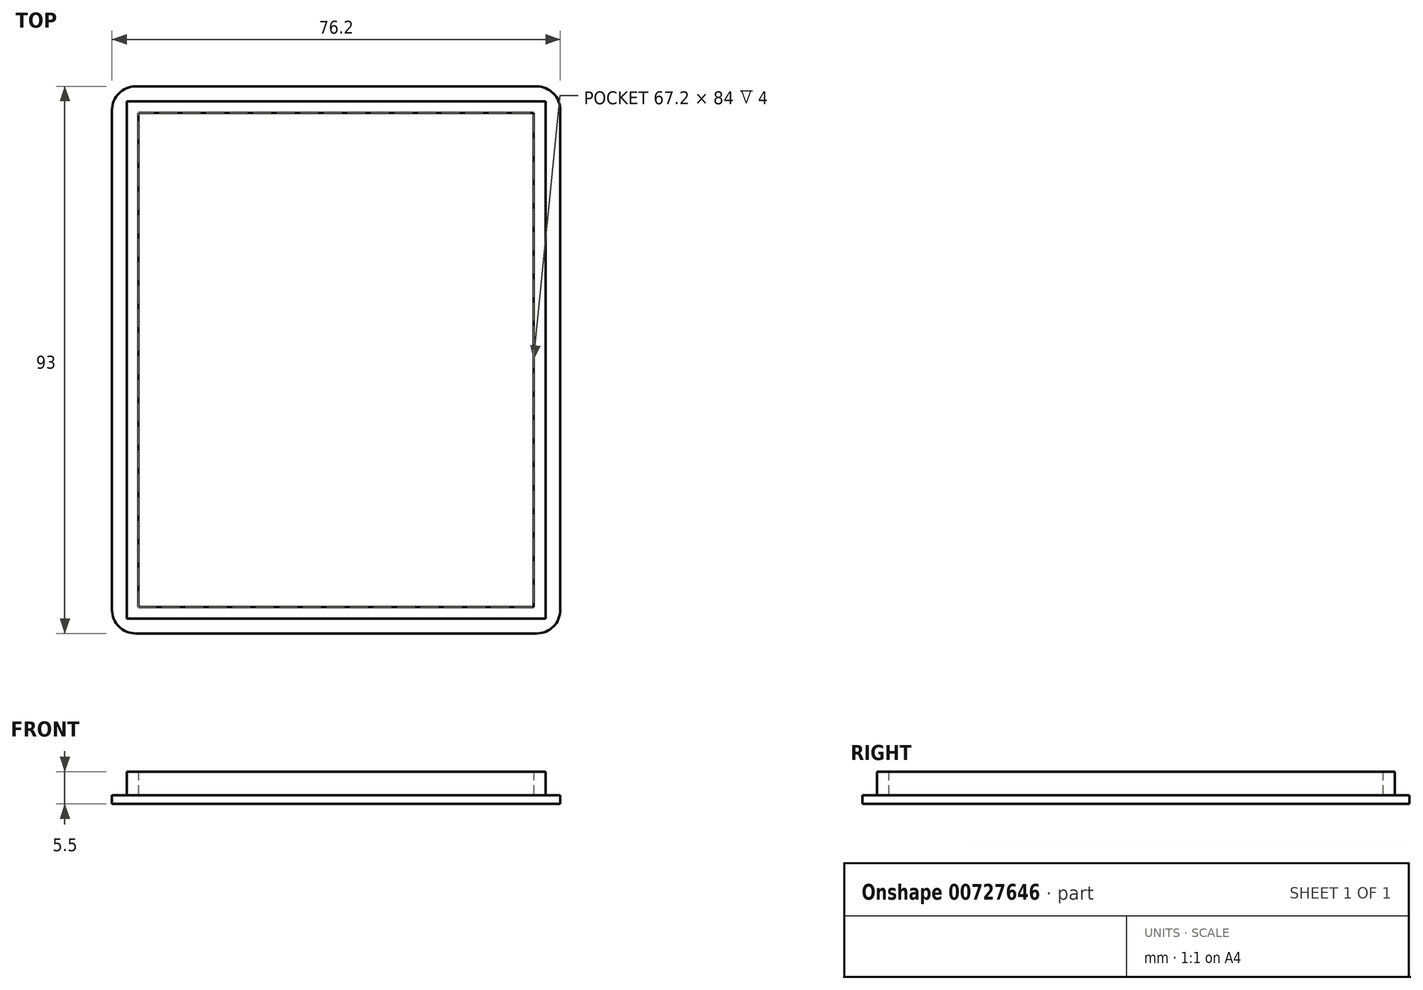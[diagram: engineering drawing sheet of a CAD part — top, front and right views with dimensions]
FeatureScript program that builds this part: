
annotation { "Feature Type Name" : "Feature", "Feature Type Description" : "" }
export const myFeature = defineFeature(function(context is Context, id is Id, definition is map)
    precondition{}
    {
        {
            var Q0;
            Q0=qCreatedBy(makeId("Top.planeOp"),FACE);
            var sketch = newSketch(context, id + "F0", { "sketchPlane" : qUnion([Q0])});
            skLineSegment(sketch, "E0", {"start": v(-32.71, 37.82) * mm, "end": v(35.49, 37.82) * mm});
            skLineSegment(sketch, "E1", {"start": v(-36.71, 33.82) * mm, "end": v(-36.71, -51.18) * mm});
            skLineSegment(sketch, "E2", {"start": v(-32.71, -55.18) * mm, "end": v(35.49, -55.18) * mm});
            skLineSegment(sketch, "E3", {"start": v(39.49, -51.18) * mm, "end": v(39.49, 33.82) * mm});
            skArc(sketch, "E4", {"start": v(39.49, 33.82) * mm, "mid": v(38.31, 36.65) * mm, "end": v(35.49, 37.82) * mm});
            skArc(sketch, "E5", {"start": v(-32.71, 37.82) * mm, "mid": v(-35.54, 36.65) * mm, "end": v(-36.71, 33.82) * mm});
            skArc(sketch, "E6", {"start": v(-36.71, -51.18) * mm, "mid": v(-35.54, -54.01) * mm, "end": v(-32.71, -55.18) * mm});
            skArc(sketch, "E7", {"start": v(39.49, -51.18) * mm, "mid": v(38.31, -54.01) * mm, "end": v(35.49, -55.18) * mm});
            skLineSegment(sketch, "E8", {"start": v(36.99, 35.32) * mm, "end": v(36.99, -52.68) * mm});
            skLineSegment(sketch, "E9", {"start": v(-34.21, -52.68) * mm, "end": v(36.99, -52.68) * mm});
            skLineSegment(sketch, "E10", {"start": v(-34.21, 35.32) * mm, "end": v(-34.21, -52.68) * mm});
            skLineSegment(sketch, "E11", {"start": v(-34.21, 35.32) * mm, "end": v(36.99, 35.32) * mm});
            skSolve(sketch);
        }
        {
            var Q0;
            Q0=makeQuery(id+"F0.imprint","IMPRINT",FACE,{"disambiguationData":[TD([[makeQuery(id+"F0.imprint","IMPRINT",EDGE,{"derivedFrom":sQuery(id+"F0.wireOp",EDGE,"E8")}),-1.0]])]});
            var Q1;
            Q1=makeQuery(id+"F0.imprint","IMPRINT",FACE,{"disambiguationData":[TD([[makeQuery(id+"F0.imprint","IMPRINT",EDGE,{"derivedFrom":sQuery(id+"F0.wireOp",EDGE,"E0")}),-1.0]])]});
            extrude(context, id + "F1", {"entities" : qUnion([Q0, Q1]), "depth" : 1.5 * mm, "offsetDistance" : 25 * mm});
        }
        {
            var Q0;
            Q0=makeQuery(id+"F1.opExtrude","CAP_FACE",FACE,{"disambiguationData":[OSD([sQuery(id+"F0.wireOp",EDGE,"E0"),sQuery(id+"F0.wireOp",EDGE,"E1"),sQuery(id+"F0.wireOp",EDGE,"E2"),sQuery(id+"F0.wireOp",EDGE,"E3"),sQuery(id+"F0.wireOp",EDGE,"E4"),sQuery(id+"F0.wireOp",EDGE,"E5"),sQuery(id+"F0.wireOp",EDGE,"E6"),sQuery(id+"F0.wireOp",EDGE,"E7")])],"isStart":false});
            var sketch = newSketch(context, id + "F2", { "sketchPlane" : qUnion([Q0])});
            skLineSegment(sketch, "E12", {"start": v(-34.21, 35.32) * mm, "end": v(36.99, 35.32) * mm});
            skLineSegment(sketch, "E13", {"start": v(-34.21, -52.68) * mm, "end": v(36.99, -52.68) * mm});
            skLineSegment(sketch, "E14", {"start": v(-34.21, 35.32) * mm, "end": v(-34.21, -52.68) * mm});
            skLineSegment(sketch, "E15", {"start": v(36.99, -52.68) * mm, "end": v(36.99, 35.32) * mm});
            skLineSegment(sketch, "E16", {"start": v(-32.21, 33.32) * mm, "end": v(34.99, 33.32) * mm});
            skLineSegment(sketch, "E17", {"start": v(-32.21, -50.68) * mm, "end": v(34.99, -50.68) * mm});
            skLineSegment(sketch, "E18", {"start": v(-32.21, 33.32) * mm, "end": v(-32.21, -50.68) * mm});
            skLineSegment(sketch, "E19", {"start": v(34.99, -50.68) * mm, "end": v(34.99, 33.32) * mm});
            skSolve(sketch);
        }
        {
            var Q0;
            Q0=makeQuery(id+"F2.imprint","IMPRINT",FACE,{"disambiguationData":[TD([[makeQuery(id+"F2.imprint","IMPRINT",EDGE,{"derivedFrom":sQuery(id+"F2.wireOp",EDGE,"E12")}),-1.0]])]});
            extrude(context, id + "F3", {"entities" : qUnion([Q0]), "operationType" : NewBodyOperationType.ADD, "depth" : 4 * mm, "offsetDistance" : 25 * mm});
        }
    });
